# Revit family: Specialty_Equipment-Planter-Planters_Unlimited-Modern-Banded-rev
name_source: partatom
category: Specialty Equipment
units: mm (PartAtom-declared; Revit-internal decimal feet)

## family parameters
Always vertical = Yes
Cut with Voids When Loaded = No
Enable Cutting in Views = No
Maintain Annotation Orientation = No
OmniClass Number = 23.40.05.21.17
OmniClass Title = Planters
Part Type = Normal
Room Calculation Point = No
Round Connector Dimension = Use Diameter
Shared = No
Work Plane-Based = No

## types (10) — shared parameters
Assembly Code = G2050600
CD_Finish = Saucer
CD_Microsite = https://www.caddetails.com
CD_Offset = 0' - 0 1/2"
CD_Product Page URL = https://www.plantersunlimited.com
CD_Specification = https://www.plantersunlimited.com
Default Elevation = 0' - 0"
Description = Modular Planting Bed
Manufacturer = Planters Unlimited
Model = Banded Round GFRC Planter
Type Comments = Banded Round GFRC Planter
URL = https://www.plantersunlimited.com

## per-type parameters (varying)
| type | CD_Height | CD_Width |
| 21.5" Dia x19.5"H | 1' - 2" | 1' - 9 1/2" |
| 24" Dia x19.5"H | 1' - 7 1/2" | 2' - 0" |
| 24" Dia x24"H | 2' - 0" | 2' - 0" |
| 27" Dia x24"H | 2' - 0" | 2' - 3" |
| 31" Dia x25"H | 2' - 1" | 2' - 7" |
| 33" Dia x15"H | 1' - 3" | 2' - 9" |
| 36" Dia x29"H | 2' - 5" | 3' - 0" |
| 36" Dia x39"H | 3' - 3" | 3' - 0" |
| 36.5" Dia x23"H | 1' - 11" | 3' - 0 1/2" |
| 48" Dia x38"H | 3' - 2" | 4' - 0" |

## geometry (parser evidence)
native form markers: Sweep x2
no freeform markers — native parametric forms only
